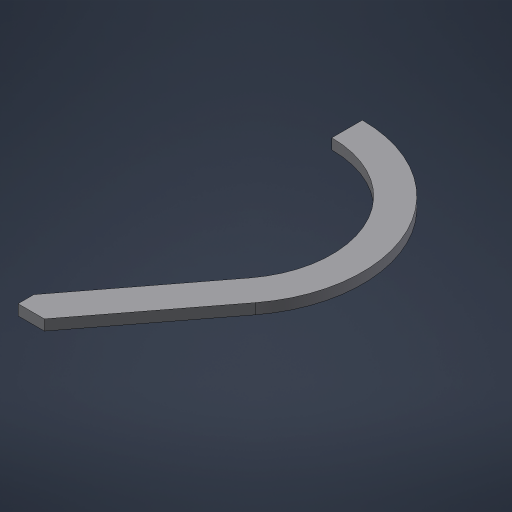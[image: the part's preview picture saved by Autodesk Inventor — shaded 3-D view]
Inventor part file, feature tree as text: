
AUTODESK INVENTOR PART (.ipt)
format: ipt  version: 2023.5 (Build 275446000, 446)  size: 376,832 bytes
history: native  units: mm
features: extrude x1, sketch x1
ambient origin geometry x8: Origin, YZ Plane, XZ Plane, XY Plane, X Axis, Y Axis, Z Axis, Center Point
bodies: Volumenkörper1 (feature_tree)
feature tree (2):
  extrude  "Extrusion1"  Depth=5.0mm
  sketch  "Skizze1"  dims[d0=3.0mm d1=5.0mm d2=25.0mm d3=60.0mm d4=2.0mm d5=0.0mm]
